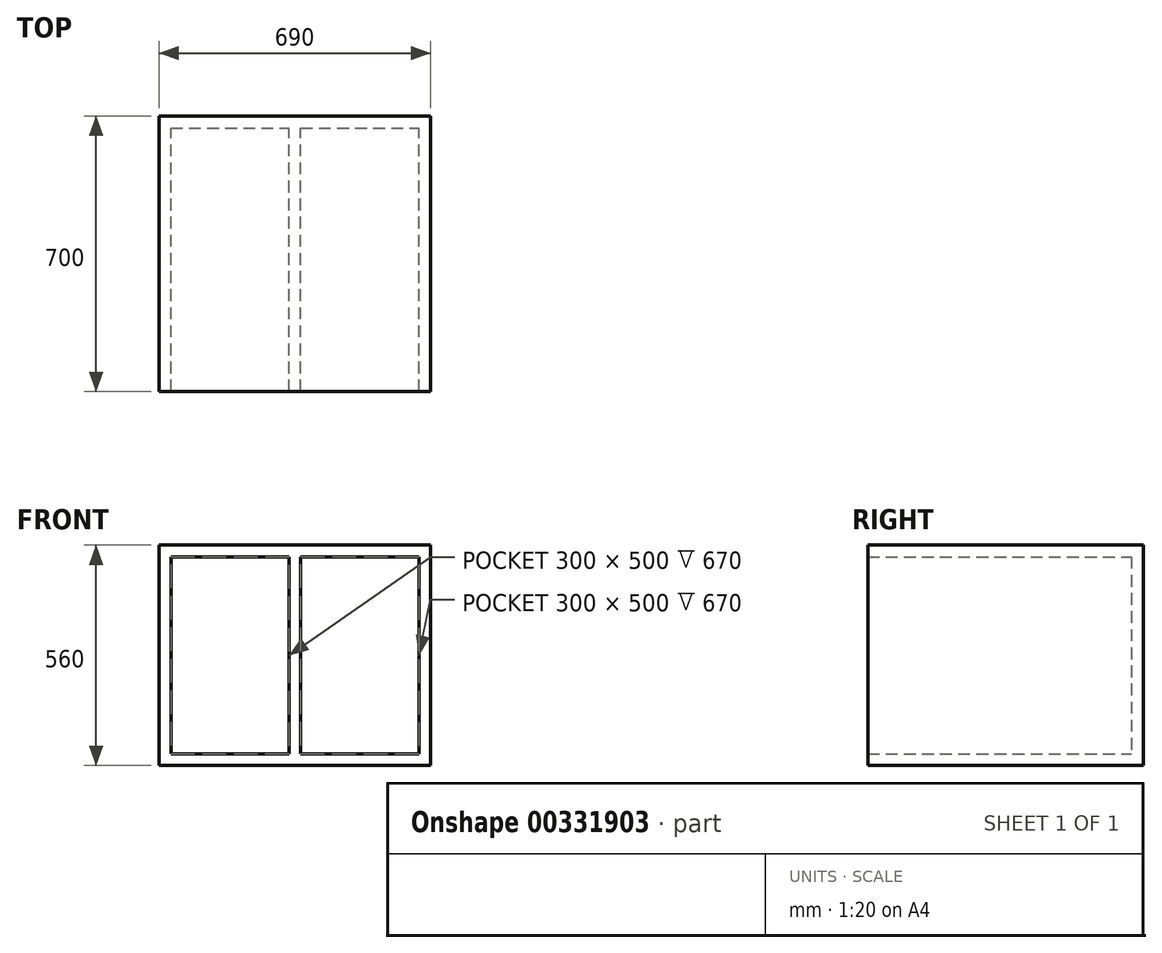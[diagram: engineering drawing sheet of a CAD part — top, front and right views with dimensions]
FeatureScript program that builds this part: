
annotation { "Feature Type Name" : "Feature", "Feature Type Description" : "" }
export const myFeature = defineFeature(function(context is Context, id is Id, definition is map)
    precondition{}
    {
        {
            var Q0;
            Q0=qCreatedBy(makeId("Front.planeOp"),FACE);
            var sketch = newSketch(context, id + "F0", { "sketchPlane" : qUnion([Q0])});
            skLineSegment(sketch, "E0.bottom", {"start": v(345, -280) * mm, "end": v(-345, -280) * mm});
            skLineSegment(sketch, "E0.top", {"start": v(345, 280) * mm, "end": v(-345, 280) * mm});
            skLineSegment(sketch, "E0.left", {"start": v(345, -280) * mm, "end": v(345, 280) * mm});
            skLineSegment(sketch, "E0.right", {"start": v(-345, -280) * mm, "end": v(-345, 280) * mm});
            skPoint(sketch, "E0.middle", {"position": v(0, 0) * mm});
            skLineSegment(sketch, "E1.bottom", {"start": v(-315, 250) * mm, "end": v(-15, 250) * mm});
            skLineSegment(sketch, "E1.top", {"start": v(-315, -250) * mm, "end": v(-15, -250) * mm});
            skLineSegment(sketch, "E1.left", {"start": v(-315, 250) * mm, "end": v(-315, -250) * mm});
            skLineSegment(sketch, "E1.right", {"start": v(-15, 250) * mm, "end": v(-15, -250) * mm});
            skPoint(sketch, "E1.middle", {"position": v(-165, 0) * mm});
            skLineSegment(sketch, "E2.bottom", {"start": v(15, 250) * mm, "end": v(315, 250) * mm});
            skLineSegment(sketch, "E2.top", {"start": v(15, -250) * mm, "end": v(315, -250) * mm});
            skLineSegment(sketch, "E2.left", {"start": v(15, 250) * mm, "end": v(15, -250) * mm});
            skLineSegment(sketch, "E2.right", {"start": v(315, 250) * mm, "end": v(315, -250) * mm});
            skPoint(sketch, "E2.middle", {"position": v(165, 0) * mm});
            skSolve(sketch);
        }
        {
            var Q0;
            Q0=makeQuery(id+"F0.imprint","IMPRINT",FACE,{"disambiguationData":[TD([[makeQuery(id+"F0.imprint","IMPRINT",EDGE,{"derivedFrom":sQuery(id+"F0.wireOp",EDGE,"E0.bottom")}),-1.0]])]});
            extrude(context, id + "F1", {"entities" : qUnion([Q0]), "depth" : 700 * mm});
        }
        {
            var Q0;
            Q0=makeQuery(id+"F0.imprint","IMPRINT",FACE,{"disambiguationData":[TD([[makeQuery(id+"F0.imprint","IMPRINT",EDGE,{"derivedFrom":sQuery(id+"F0.wireOp",EDGE,"E1.bottom")}),-1.0]])]});
            var Q1;
            Q1=makeQuery(id+"F0.imprint","IMPRINT",FACE,{"disambiguationData":[TD([[makeQuery(id+"F0.imprint","IMPRINT",EDGE,{"derivedFrom":sQuery(id+"F0.wireOp",EDGE,"E2.bottom")}),-1.0]])]});
            extrude(context, id + "F2", {"entities" : qUnion([Q0, Q1]), "operationType" : NewBodyOperationType.ADD, "depth" : 30 * mm});
        }
    });
